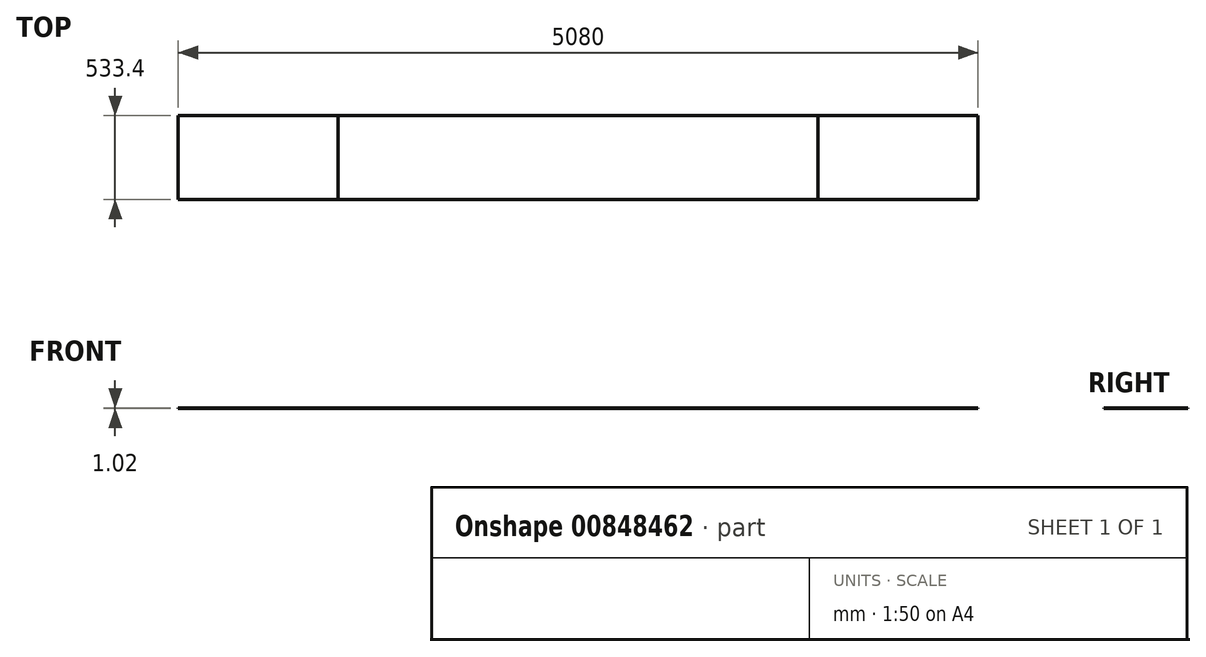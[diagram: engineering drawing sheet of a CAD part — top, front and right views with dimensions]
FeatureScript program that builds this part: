
annotation { "Feature Type Name" : "Feature", "Feature Type Description" : "" }
export const myFeature = defineFeature(function(context is Context, id is Id, definition is map)
    precondition{}
    {
        {
            var Q0;
            Q0=qCreatedBy(makeId("Top.planeOp"),FACE);
            var sketch = newSketch(context, id + "F0", { "sketchPlane" : qUnion([Q0])});
            skLineSegment(sketch, "E0.bottom", {"start": v(-2429.26, 96.34) * mm, "end": v(-1413.26, 96.34) * mm});
            skLineSegment(sketch, "E0.top", {"start": v(-2429.26, -437.06) * mm, "end": v(-1413.26, -437.06) * mm});
            skLineSegment(sketch, "E0.left", {"start": v(-2429.26, 96.34) * mm, "end": v(-2429.26, -437.06) * mm});
            skLineSegment(sketch, "E0.right", {"start": v(-1413.26, 96.34) * mm, "end": v(-1413.26, -437.06) * mm});
            skLineSegment(sketch, "E1.bottom", {"start": v(-1413.26, 96.34) * mm, "end": v(1634.74, 96.34) * mm});
            skLineSegment(sketch, "E1.top", {"start": v(-1413.26, -437.06) * mm, "end": v(1634.74, -437.06) * mm});
            skLineSegment(sketch, "E1.right", {"start": v(1634.74, 96.34) * mm, "end": v(1634.74, -437.06) * mm});
            skLineSegment(sketch, "E2.bottom", {"start": v(1634.74, 96.34) * mm, "end": v(2650.74, 96.34) * mm});
            skLineSegment(sketch, "E2.top", {"start": v(1634.74, -437.06) * mm, "end": v(2650.74, -437.06) * mm});
            skLineSegment(sketch, "E2.right", {"start": v(2650.74, 96.34) * mm, "end": v(2650.74, -437.06) * mm});
            skSolve(sketch);
        }
        {
            var Q0;
            Q0=makeQuery(id+"F0.imprint","IMPRINT",FACE,{"disambiguationData":[TD([[makeQuery(id+"F0.imprint","IMPRINT",EDGE,{"derivedFrom":sQuery(id+"F0.wireOp",EDGE,"E1.bottom")}),-1.0]])]});
            extrude(context, id + "F1", {"entities" : qUnion([Q0]), "depth" : 1.02 * mm, "offsetDistance" : 25.4 * mm});
        }
        {
            var Q0;
            Q0=makeQuery(id+"F0.imprint","IMPRINT",FACE,{"disambiguationData":[TD([[makeQuery(id+"F0.imprint","IMPRINT",EDGE,{"derivedFrom":sQuery(id+"F0.wireOp",EDGE,"E0.bottom")}),-1.0]])]});
            var Q1;
            Q1=makeQuery(id+"F0.imprint","IMPRINT",FACE,{"disambiguationData":[TD([[makeQuery(id+"F0.imprint","IMPRINT",EDGE,{"derivedFrom":sQuery(id+"F0.wireOp",EDGE,"E2.bottom")}),-1.0]])]});
            extrude(context, id + "F2", {"entities" : qUnion([Q0, Q1]), "depth" : 1.02 * mm, "offsetDistance" : 25.4 * mm});
        }
    });
